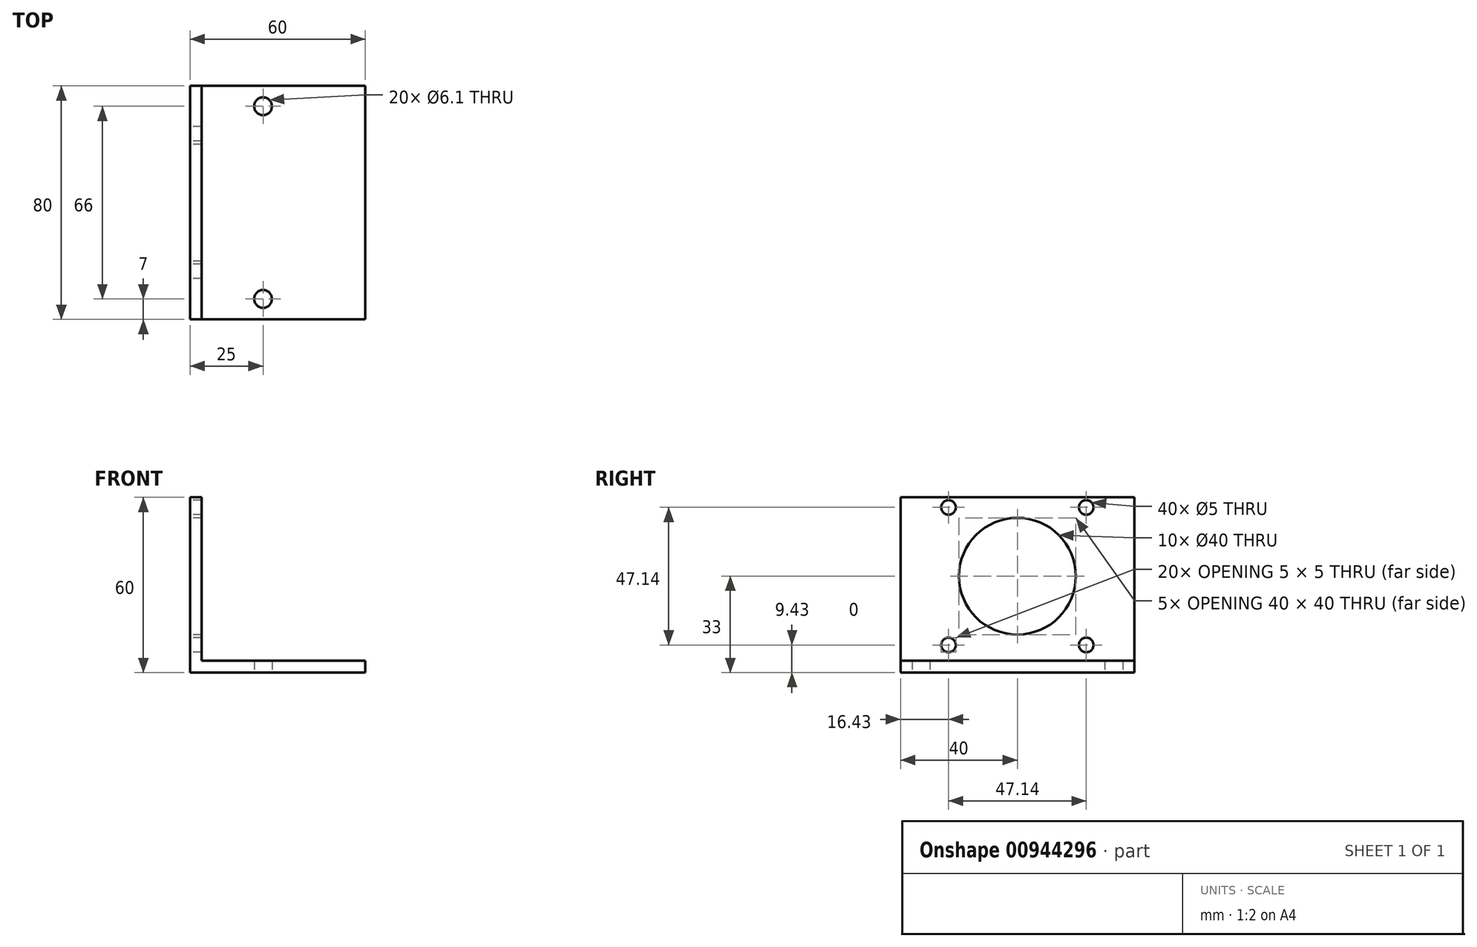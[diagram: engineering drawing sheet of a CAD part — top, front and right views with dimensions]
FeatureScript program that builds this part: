
annotation { "Feature Type Name" : "Feature", "Feature Type Description" : "" }
export const myFeature = defineFeature(function(context is Context, id is Id, definition is map)
    precondition{}
    {
        {
            var Q0;
            Q0=qCreatedBy(makeId("Front.planeOp"),FACE);
            var sketch = newSketch(context, id + "F0", { "sketchPlane" : qUnion([Q0])});
            skLineSegment(sketch, "E0", {"start": v(0, 0) * mm, "end": v(0, 60) * mm});
            skLineSegment(sketch, "E1", {"start": v(0, 60) * mm, "end": v(4, 60) * mm});
            skLineSegment(sketch, "E2", {"start": v(4, 60) * mm, "end": v(4, 4) * mm});
            skLineSegment(sketch, "E3", {"start": v(4, 4) * mm, "end": v(60, 4) * mm});
            skLineSegment(sketch, "E4", {"start": v(60, 4) * mm, "end": v(60, 0) * mm});
            skLineSegment(sketch, "E5", {"start": v(60, 0) * mm, "end": v(0, 0) * mm});
            skSolve(sketch);
        }
        {
            var Q0;
            Q0=qSketchRegion(id+"F0",true);
            extrude(context, id + "F1", {"entities" : qUnion([Q0]), "depth" : 80 * mm, "offsetDistance" : 25 * mm});
        }
        {
            var Q0;
            Q0=makeQuery(id+"F1.opExtrude","SWEPT_FACE",FACE,{"disambiguationData":[OSD([sQuery(id+"F0.wireOp",EDGE,"E0")])]});
            var sketch = newSketch(context, id + "F2", { "sketchPlane" : qUnion([Q0])});
            skLineSegment(sketch, "E6", {"start": v(40, 60) * mm, "end": v(40, 0) * mm, "construction": true});
            skLineSegment(sketch, "E7", {"start": v(0, 33) * mm, "end": v(80, 33) * mm, "construction": true});
            skPoint(sketch, "E8.middle", {"position": v(40, 33) * mm});
            skCircle(sketch, "E9", {"center": v(16.43, 56.57) * mm, "radius": 2.5 * mm});
            skCircle(sketch, "E10", {"center": v(40, 33) * mm, "radius": 20 * mm});
            skCircle(sketch, "E11.MirrorC", {"center": v(63.57, 56.57) * mm, "radius": 2.5 * mm});
            skCircle(sketch, "E12.MirrorC", {"center": v(16.43, 9.43) * mm, "radius": 2.5 * mm});
            skCircle(sketch, "E13.MirrorC", {"center": v(63.57, 9.43) * mm, "radius": 2.5 * mm});
            skSolve(sketch);
        }
        {
            var Q0;
            Q0=makeQuery(id+"F1.opExtrude","SWEPT_FACE",FACE,{"disambiguationData":[OSD([sQuery(id+"F0.wireOp",EDGE,"E5")])]});
            var sketch = newSketch(context, id + "F3", { "sketchPlane" : qUnion([Q0])});
            skLineSegment(sketch, "E14", {"start": v(25, 80) * mm, "end": v(25, 0) * mm, "construction": true});
            skCircle(sketch, "E15", {"center": v(25, 73) * mm, "radius": 3.05 * mm});
            skCircle(sketch, "E16", {"center": v(25, 7) * mm, "radius": 3.05 * mm});
            skSolve(sketch);
        }
        {
            var Q0;
            Q0=qSketchRegion(id+"F3",true);
            extrude(context, id + "F4", {"entities" : qUnion([Q0]), "operationType" : NewBodyOperationType.REMOVE, "oppositeDirection" : true, "depth" : 25 * mm, "offsetDistance" : 25 * mm});
        }
        {
            var Q0;
            Q0=qSketchRegion(id+"F2",true);
            extrude(context, id + "F5", {"entities" : qUnion([Q0]), "operationType" : NewBodyOperationType.REMOVE, "endBound" : BoundingType.UP_TO_NEXT, "oppositeDirection" : true, "depth" : 25 * mm, "offsetDistance" : 25 * mm});
        }
    });
